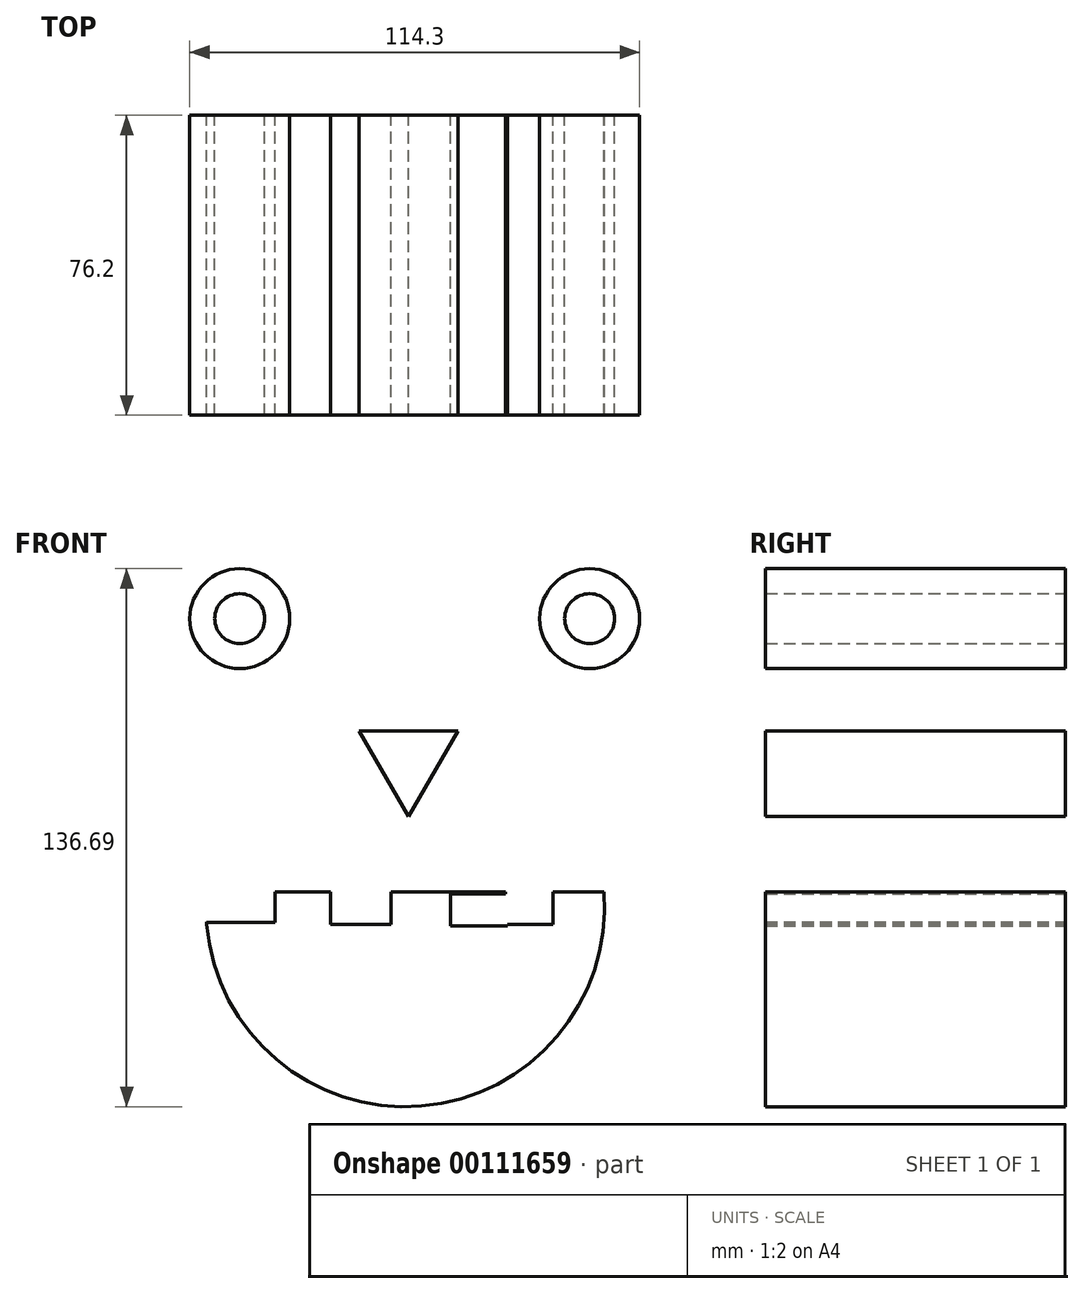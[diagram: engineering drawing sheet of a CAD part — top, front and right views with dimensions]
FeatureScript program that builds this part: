
annotation { "Feature Type Name" : "Feature", "Feature Type Description" : "" }
export const myFeature = defineFeature(function(context is Context, id is Id, definition is map)
    precondition{}
    {
        {
            var Q0;
            Q0=qCreatedBy(makeId("Front.planeOp"),FACE);
            var sketch = newSketch(context, id + "F0", { "sketchPlane" : qUnion([Q0])});
            skCircle(sketch, "E0", {"center": v(-42.83, 35.78) * mm, "radius": 12.7 * mm});
            skCircle(sketch, "E1", {"center": v(46.07, 35.78) * mm, "radius": 12.7 * mm});
            skCircle(sketch, "E2.cCircle", {"center": v(0, 0) * mm, "radius": 7.26 * mm, "construction": true});
            skLineSegment(sketch, "E2.0", {"start": v(12.57, 7.27) * mm, "end": v(0, -14.52) * mm});
            skLineSegment(sketch, "E2.1", {"start": v(0, -14.52) * mm, "end": v(-12.58, 7.26) * mm});
            skLineSegment(sketch, "E2.2", {"start": v(-12.58, 7.26) * mm, "end": v(12.57, 7.27) * mm});
            skPoint(sketch, "E2.0.midPoint", {"position": v(6.29, -3.63) * mm});
            skLineSegment(sketch, "E3", {"start": v(-43.67, -33.63) * mm, "end": v(49.64, -33.63) * mm});
            skArc(sketch, "E4", {"start": v(-51.26, -41.9) * mm, "mid": v(3.31, -88.04) * mm, "end": v(49.64, -33.63) * mm});
            skCircle(sketch, "E5", {"center": v(-42.83, 35.78) * mm, "radius": 6.35 * mm});
            skCircle(sketch, "E6", {"center": v(46.07, 35.78) * mm, "radius": 6.35 * mm});
            skLineSegment(sketch, "E7.bottom", {"start": v(-43.67, -33.63) * mm, "end": v(-33.87, -33.63) * mm});
            skLineSegment(sketch, "E7.top", {"start": v(-51.29, -41.37) * mm, "end": v(-33.87, -41.37) * mm});
            skLineSegment(sketch, "E7.left", {"start": v(-51.29, -41.25) * mm, "end": v(-51.29, -41.37) * mm});
            skLineSegment(sketch, "E7.right", {"start": v(-33.87, -33.63) * mm, "end": v(-33.87, -41.37) * mm});
            skLineSegment(sketch, "E8.bottom", {"start": v(-33.87, -41.37) * mm, "end": v(-19.84, -41.37) * mm});
            skLineSegment(sketch, "E8.top", {"start": v(-33.87, -33.63) * mm, "end": v(-19.84, -33.63) * mm});
            skLineSegment(sketch, "E8.left", {"start": v(-33.87, -41.37) * mm, "end": v(-33.87, -33.63) * mm});
            skLineSegment(sketch, "E8.right", {"start": v(-19.84, -41.37) * mm, "end": v(-19.84, -33.63) * mm});
            skLineSegment(sketch, "E9.bottom", {"start": v(-19.84, -33.63) * mm, "end": v(-4.35, -33.63) * mm});
            skLineSegment(sketch, "E9.top", {"start": v(-19.84, -41.85) * mm, "end": v(-4.35, -41.85) * mm});
            skLineSegment(sketch, "E9.left", {"start": v(-19.84, -33.63) * mm, "end": v(-19.84, -41.85) * mm});
            skLineSegment(sketch, "E9.right", {"start": v(-4.35, -33.63) * mm, "end": v(-4.35, -41.85) * mm});
            skLineSegment(sketch, "E10.bottom", {"start": v(-4.35, -41.85) * mm, "end": v(10.64, -41.85) * mm});
            skLineSegment(sketch, "E10.top", {"start": v(-4.35, -33.63) * mm, "end": v(10.64, -33.63) * mm});
            skLineSegment(sketch, "E10.left", {"start": v(-4.35, -41.85) * mm, "end": v(-4.35, -33.63) * mm});
            skLineSegment(sketch, "E10.right", {"start": v(10.64, -41.85) * mm, "end": v(10.64, -33.63) * mm});
            skLineSegment(sketch, "E11.bottom", {"start": v(10.64, -34.11) * mm, "end": v(25.16, -34.11) * mm});
            skLineSegment(sketch, "E11.top", {"start": v(10.64, -42.34) * mm, "end": v(25.16, -42.34) * mm});
            skLineSegment(sketch, "E11.left", {"start": v(10.64, -34.11) * mm, "end": v(10.64, -42.34) * mm});
            skLineSegment(sketch, "E11.right", {"start": v(25.16, -34.11) * mm, "end": v(25.16, -42.34) * mm});
            skLineSegment(sketch, "E12.bottom", {"start": v(24.68, -41.85) * mm, "end": v(36.77, -41.85) * mm});
            skLineSegment(sketch, "E12.top", {"start": v(24.68, -33.63) * mm, "end": v(36.77, -33.63) * mm});
            skLineSegment(sketch, "E12.left", {"start": v(24.68, -41.85) * mm, "end": v(24.68, -33.63) * mm});
            skLineSegment(sketch, "E12.right", {"start": v(36.77, -41.85) * mm, "end": v(36.77, -33.63) * mm});
            skPoint(sketch, "E13.visualSharp", {"position": v(-51.29, -33.63) * mm});
            skArc(sketch, "E13.filletArc", {"start": v(-43.67, -33.63) * mm, "mid": v(-49.28, -36.1) * mm, "end": v(-51.26, -41.9) * mm});
            skArc(sketch, "E14.filletArc", {"start": v(-43.67, -33.63) * mm, "mid": v(-49.05, -35.86) * mm, "end": v(-51.29, -41.25) * mm});
            skSolve(sketch);
        }
        {
            var Q0;
            Q0=makeQuery(id+"F0.imprint","IMPRINT",FACE,{"disambiguationData":[TD([[makeQuery(id+"F0.imprint","IMPRINT",EDGE,{"derivedFrom":sQuery(id+"F0.wireOp",EDGE,"E2.0")}),-1.0]])]});
            var Q1;
            Q1=makeQuery(id+"F0.imprint","IMPRINT",FACE,{"disambiguationData":[TD([[makeQuery(id+"F0.imprint","IMPRINT",EDGE,{"derivedFrom":sQuery(id+"F0.wireOp",EDGE,"E0")}),1.0]])]});
            var Q2;
            Q2=makeQuery(id+"F0.imprint","IMPRINT",FACE,{"disambiguationData":[TD([[makeQuery(id+"F0.imprint","IMPRINT",EDGE,{"derivedFrom":sQuery(id+"F0.wireOp",EDGE,"E1")}),1.0]])]});
            var Q3;
            {var subQ0=sQuery(id+"F0.wireOp",EDGE,"E7.left");Q3=makeQuery(id+"F0.imprint","IMPRINT",FACE,{"disambiguationData":[TD([[makeQuery(id+"F0.imprint","IMPRINT",EDGE,{"derivedFrom":subQ0}),1.0]])]});}
            var Q4;
            {var subQ0=sQuery(id+"F0.wireOp",EDGE,"E10.right");Q4=makeQuery(id+"F0.imprint","IMPRINT",FACE,{"disambiguationData":[TD([[makeQuery(id+"F0.imprint","IMPRINT",EDGE,{"derivedFrom":subQ0}),-1.0]])]});}
            var Q5;
            Q5=makeQuery(id+"F0.imprint","IMPRINT",FACE,{"disambiguationData":[TD([[makeQuery(id+"F0.imprint","IMPRINT",EDGE,{"derivedFrom":sQuery(id+"F0.wireOp",EDGE,"E7.bottom")}),-1.0]])]});
            var Q6;
            {var subQ0=sQuery(id+"F0.wireOp",EDGE,"E8.bottom");Q6=makeQuery(id+"F0.imprint","IMPRINT",FACE,{"disambiguationData":[TD([[makeQuery(id+"F0.imprint","IMPRINT",EDGE,{"derivedFrom":subQ0}),1.0]])]});}
            var Q7;
            {var subQ2=sQuery(id+"F0.wireOp",EDGE,"E9.bottom");Q7=makeQuery(id+"F0.imprint","IMPRINT",FACE,{"disambiguationData":[TD([[makeQuery(id+"F0.imprint","IMPRINT",EDGE,{"derivedFrom":subQ2}),-1.0]])]});}
            var Q8;
            {var subQ4=sQuery(id+"F0.wireOp",EDGE,"E12.top");Q8=makeQuery(id+"F0.imprint","IMPRINT",FACE,{"disambiguationData":[TD([[makeQuery(id+"F0.imprint","IMPRINT",EDGE,{"derivedFrom":subQ4}),-1.0]])]});}
            var Q9;
            {var subQ1=sQuery(id+"F0.wireOp",EDGE,"E10.bottom");Q9=makeQuery(id+"F0.imprint","IMPRINT",FACE,{"disambiguationData":[TD([[makeQuery(id+"F0.imprint","IMPRINT",EDGE,{"derivedFrom":subQ1}),1.0]])]});}
            var Q10;
            {var subQ6=sQuery(id+"F0.wireOp",EDGE,"E4");Q10=makeQuery(id+"F0.imprint","IMPRINT",FACE,{"disambiguationData":[TD([[makeQuery(id+"F0.imprint","IMPRINT",EDGE,{"derivedFrom":subQ6}),1.0]])]});}
            extrude(context, id + "F1", {"entities" : qUnion([Q0, Q1, Q2, Q3, Q4, Q5, Q6, Q7, Q8, Q9, Q10]), "depth" : 76.2 * mm});
        }
    });
